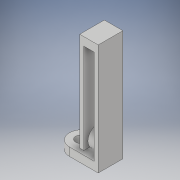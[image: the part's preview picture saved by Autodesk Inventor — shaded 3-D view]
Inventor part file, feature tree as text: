
AUTODESK INVENTOR PART (.ipt)
format: ipt  version: 2018 (Build 220112000, 112)  size: 178,688 bytes
history: native  units: in
note: dims shown in document units (in); Inventor stores cm internally (conversion verified against a paired STEP export)
features: extrude x7, sketch x7, fillet x1
ambient origin geometry x8: Origin, YZ Plane, XZ Plane, XY Plane, X Axis, Y Axis, Z Axis, Center Point
bodies: Solid1 (feature_tree)
feature tree (15):
  extrude  "Extrusion1"  Depth=0.1772in
  extrude  "Extrusion2"  Depth=0.0394in
  extrude  "Extrusion3"  Depth=0.8661in TaperAngle=0.0deg
  extrude  "Extrusion4"  Depth=0.0787in
  extrude  "Extrusion5"  Depth=0.0984in
  extrude  "Extrusion6"  Depth=0.1378in
  extrude  "Extrusion7"  Depth=0.1181in
  fillet  "Fillet1"  Radius=0.0787in
  sketch  "Sketch1"  dims[d0=0.2362in d1=0.1772in]
  sketch  "Sketch2"  dims[d2=0.0787in d3=0.0in d4=0.0394in]
  sketch  "Sketch3"  dims[d5=0.0394in d6=0.8661in d7=0.0in]
  sketch  "Sketch4"  dims[d8=0.1181in d9=0.0in d10=0.0787in]
  sketch  "Sketch5"  dims[d11=0.3543in d12=0.0in d13=0.0984in]
  sketch  "Sketch6"  dims[d14=0.1378in d15=0.0in d16=0.689in]
  sketch  "Sketch7"  dims[d17=0.0984in d18=0.1969in d19=0.0787in d20=0.0787in d21=0.0in d23=0.0984in d24=0.0787in d25=0.689in d26=0.0787in d27=0.0in d28=0.1181in]
